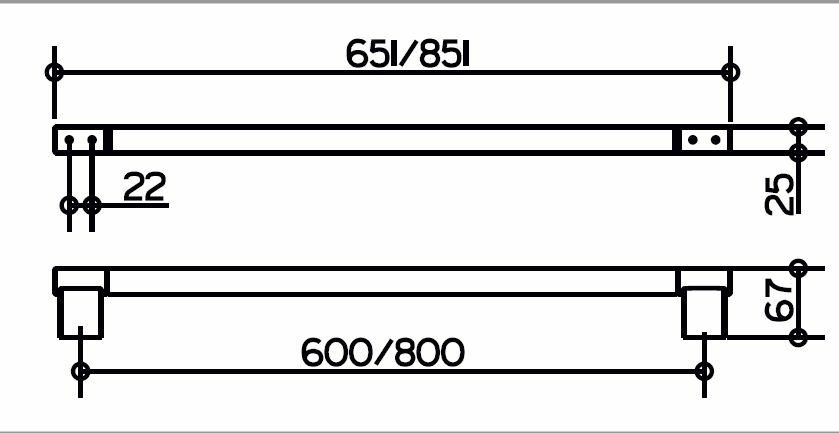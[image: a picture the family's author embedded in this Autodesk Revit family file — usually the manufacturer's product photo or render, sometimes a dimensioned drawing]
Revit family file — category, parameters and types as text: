
# Revit family: KEUCO_14988010000_
name_source: partatom
category: Generic Models
revit_build: Autodesk Revit 2016 (Build: 20150220_1215(x64)
units: mm (PartAtom-declared; Revit-internal decimal feet)

## family parameters
Always vertical = No
Can host rebar = No
Cut with Voids When Loaded = No
Part Type = Normal
Room Calculation Point = No
Round Connector Dimension = Use Diameter
Shared = No
Work Plane-Based = Yes

## types (3) — shared parameters
Default Elevation = 1219 mm
Description = wandhängend
Fassungsvermögen: 30 l
Gewicht = 2.718
Kategorie = ACC
Manufacturer = KEUCO
Rail Length = 851 mm  [stored 2.79199 ft]
Serie = Plan
URL = https://www.keuco.com

## per-type parameters (varying)
| type | Ausschreibungstext | Stange Material |
| 14988070000 | KEUCO PLAN Abfallsammler 14988070000
Abfallsammler aus hochwertigem Edelstahl 
zur Wandmontage, 30l Fassungsvermögen
Höhe 493 mm, Breite 391 mm, Ausladung 235 mm
Der Abfallsammler wird verdeckt angebracht
Lieferung inkl. korrosionsfreiem Befestigungsmaterial | Edelstahl |
| 14988010000 | KEUCO PLAN Abfallsammler 14988010000
Abfallsammler in Chrom-finish (Edelstahl poliert) 
zur Wandmontage, 30l Fassungsvermögen
Höhe 493 mm, Breite 391 mm, Ausladung 235 mm
Der Abfallsammler wird verdeckt angebracht
Lieferung inkl. korrosionsfreiem Befestigungsmaterial | Verchromt |
| 14988170000 | KEUCO PLAN Abfallsammler 14988170000
Abfallsammler aus silber-eloxiertem Aluminium (E6 EV1) 
zur Wandmontage, 30l Fassungsvermögen
Höhe 493 mm, Breite 391 mm, Ausladung 235 mm
Der Abfallsammler wird verdeckt angebracht
Lieferung inkl. korrosionsfreiem Befestigungsmaterial | Aluminium silber-eloxiert (E6 EV1) |

note: column(s) folded — value = type name in every type: Artikelnummer

note: [stored X ft] marks values corroborated as IEEE doubles in the binary element streams (Revit-internal decimal feet)

## geometry (parser evidence)
native form markers: Sweep x3
no freeform markers — native parametric forms only
